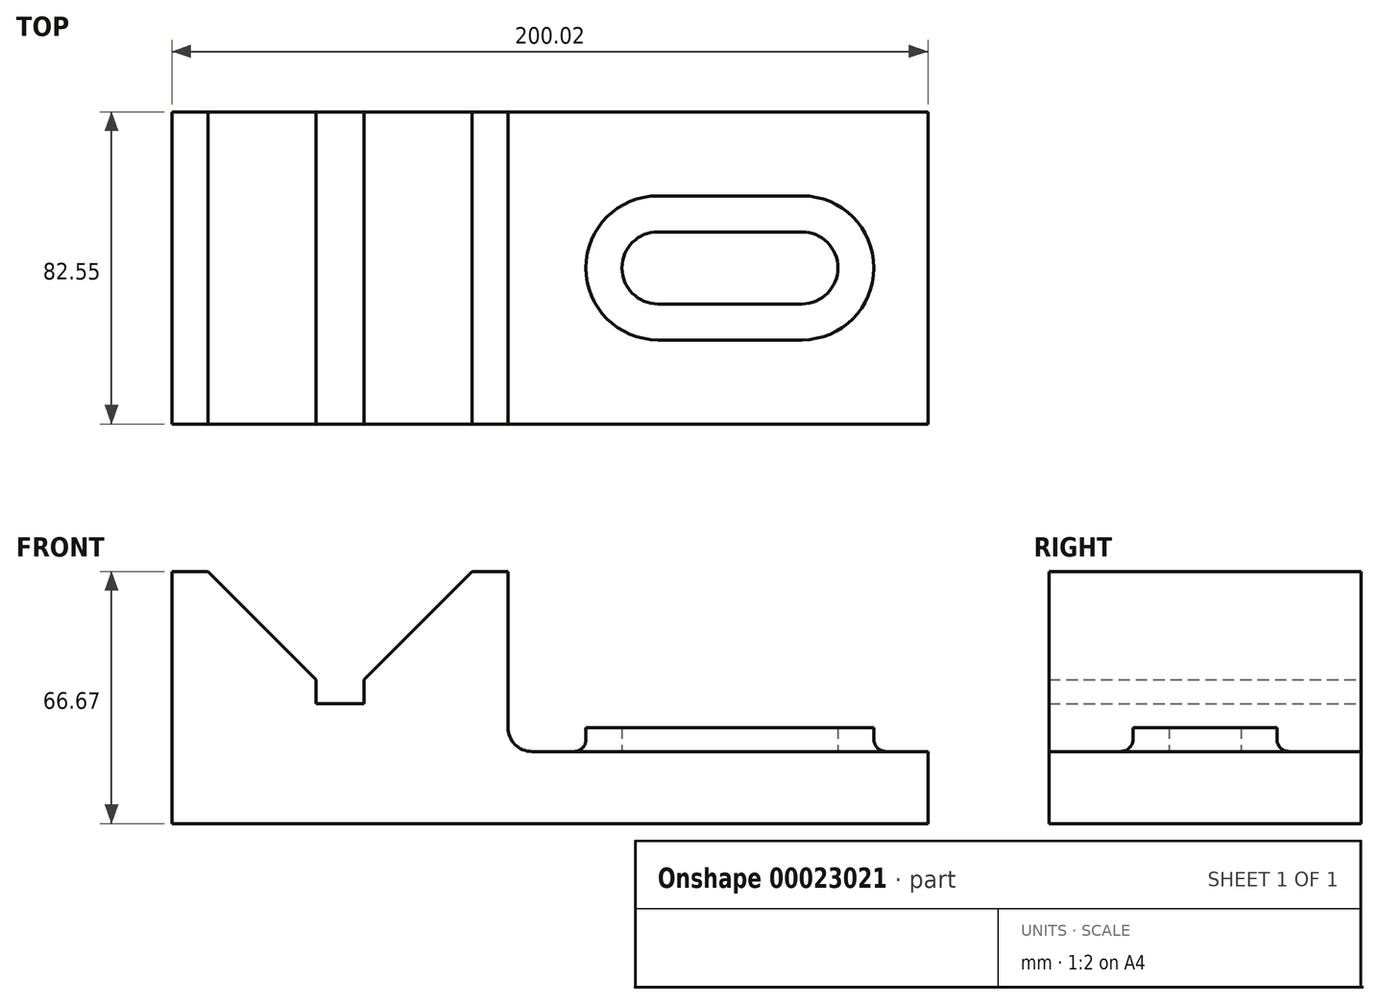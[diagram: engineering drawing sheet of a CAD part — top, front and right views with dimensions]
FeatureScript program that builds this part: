
annotation { "Feature Type Name" : "Feature", "Feature Type Description" : "" }
export const myFeature = defineFeature(function(context is Context, id is Id, definition is map)
    precondition{}
    {
        {
            var Q0;
            Q0=qCreatedBy(makeId("Front.planeOp"),FACE);
            var sketch = newSketch(context, id + "F0", { "sketchPlane" : qUnion([Q0])});
            skLineSegment(sketch, "E0", {"start": v(-103.64, -19.05) * mm, "end": v(96.38, -19.05) * mm});
            skLineSegment(sketch, "E1", {"start": v(-103.64, -19.05) * mm, "end": v(-103.64, 47.63) * mm});
            skLineSegment(sketch, "E2", {"start": v(-103.64, 47.63) * mm, "end": v(-94.12, 47.63) * mm});
            skLineSegment(sketch, "E3", {"start": v(-94.12, 47.63) * mm, "end": v(-24.27, 47.63) * mm});
            skLineSegment(sketch, "E4", {"start": v(-24.27, 47.63) * mm, "end": v(-14.74, 47.63) * mm});
            skLineSegment(sketch, "E5.bottom", {"start": v(-94.12, 47.63) * mm, "end": v(-65.54, 47.63) * mm});
            skLineSegment(sketch, "E5.top", {"start": v(-94.12, 19.05) * mm, "end": v(-65.54, 19.05) * mm});
            skLineSegment(sketch, "E5.left", {"start": v(-94.12, 47.63) * mm, "end": v(-94.12, 19.05) * mm});
            skLineSegment(sketch, "E6", {"start": v(-94.12, 47.63) * mm, "end": v(-65.54, 19.05) * mm});
            skLineSegment(sketch, "E7", {"start": v(-65.54, 19.05) * mm, "end": v(-65.54, 12.7) * mm});
            skLineSegment(sketch, "E8", {"start": v(-65.54, 12.7) * mm, "end": v(-52.84, 12.7) * mm});
            skLineSegment(sketch, "E9", {"start": v(-52.84, 12.7) * mm, "end": v(-52.84, 19.05) * mm});
            skLineSegment(sketch, "E10.bottom", {"start": v(-52.84, 19.05) * mm, "end": v(-24.27, 19.05) * mm});
            skLineSegment(sketch, "E10.top", {"start": v(-52.84, 47.63) * mm, "end": v(-24.27, 47.63) * mm});
            skLineSegment(sketch, "E10.right", {"start": v(-24.27, 19.05) * mm, "end": v(-24.27, 47.63) * mm});
            skLineSegment(sketch, "E11", {"start": v(-52.84, 19.05) * mm, "end": v(-24.27, 47.63) * mm});
            skLineSegment(sketch, "E12", {"start": v(96.38, -19.05) * mm, "end": v(96.38, 0) * mm});
            skLineSegment(sketch, "E13", {"start": v(-14.74, 47.63) * mm, "end": v(-14.74, 0) * mm});
            skLineSegment(sketch, "E14", {"start": v(-14.74, 0) * mm, "end": v(96.38, 0) * mm});
            skSolve(sketch);
        }
        {
            var Q0;
            Q0=makeQuery(id+"F0.imprint","IMPRINT",FACE,{"disambiguationData":[TD([[makeQuery(id+"F0.imprint","IMPRINT",EDGE,{"derivedFrom":sQuery(id+"F0.wireOp",EDGE,"E0")}),1.0]])]});
            var Q1;
            Q1=makeQuery(id+"F0.imprint","IMPRINT",FACE,{"disambiguationData":[TD([[makeQuery(id+"F0.imprint","IMPRINT",EDGE,{"derivedFrom":sQuery(id+"F0.wireOp",EDGE,"E5.top")}),1.0]])]});
            var Q2;
            Q2=makeQuery(id+"F0.imprint","IMPRINT",FACE,{"disambiguationData":[TD([[makeQuery(id+"F0.imprint","IMPRINT",EDGE,{"derivedFrom":sQuery(id+"F0.wireOp",EDGE,"E10.bottom")}),1.0]])]});
            extrude(context, id + "F1", {"entities" : qUnion([Q0, Q1, Q2]), "depth" : 82.55 * mm});
        }
        {
            var Q0;
            Q0=makeQuery(id+"F1.opExtrude","SWEPT_EDGE",EDGE,{"disambiguationData":[OSD([sQuery(id+"F0.wireOp",EDGE,"E13"),sQuery(id+"F0.wireOp",EDGE,"E14")])]});
            fillet(context, id + "F2", {"entities" : qUnion([Q0]), "radius" : 6.35 * mm, "tangentPropagation" : true, "allowEdgeOverflow" : false});
        }
        {
            var Q0;
            Q0=makeQuery(id+"F1.opExtrude","SWEPT_FACE",FACE,{"disambiguationData":[OSD([sQuery(id+"F0.wireOp",EDGE,"E14")])]});
            var sketch = newSketch(context, id + "F3", { "sketchPlane" : qUnion([Q0])});
            skLineSegment(sketch, "E15", {"start": v(96.38, -82.55) * mm, "end": v(96.38, 0) * mm});
            skPoint(sketch, "E16", {"position": v(96.38, -41.28) * mm});
            skArc(sketch, "E17", {"start": v(24.94, -31.75) * mm, "mid": v(15.42, -41.28) * mm, "end": v(24.94, -50.8) * mm});
            skArc(sketch, "E18", {"start": v(63.04, -50.8) * mm, "mid": v(72.57, -41.28) * mm, "end": v(63.04, -31.75) * mm});
            skArc(sketch, "E19", {"start": v(24.94, -22.23) * mm, "mid": v(5.9, -41.28) * mm, "end": v(24.94, -60.33) * mm});
            skArc(sketch, "E20", {"start": v(63.04, -60.33) * mm, "mid": v(82.1, -41.28) * mm, "end": v(63.04, -22.23) * mm});
            skLineSegment(sketch, "E21", {"start": v(24.94, -60.33) * mm, "end": v(63.04, -60.33) * mm});
            skLineSegment(sketch, "E22", {"start": v(63.04, -22.23) * mm, "end": v(24.94, -22.23) * mm});
            skLineSegment(sketch, "E23", {"start": v(24.94, -50.8) * mm, "end": v(63.04, -50.8) * mm});
            skLineSegment(sketch, "E24", {"start": v(24.94, -31.75) * mm, "end": v(63.04, -31.75) * mm});
            skPoint(sketch, "E25.start.orphan", {"position": v(-8.4, -41.28) * mm});
            skSolve(sketch);
        }
        {
            var Q0;
            Q0=makeQuery(id+"F3.imprint","IMPRINT",FACE,{"disambiguationData":[TD([[makeQuery(id+"F3.imprint","IMPRINT",EDGE,{"derivedFrom":sQuery(id+"F3.wireOp",EDGE,"E17")}),-1.0]])]});
            extrude(context, id + "F4", {"entities" : qUnion([Q0]), "operationType" : NewBodyOperationType.ADD, "depth" : 6.35 * mm});
        }
        {
            var Q0;
            Q0=makeQuery(id+"F4.opExtrude","CAP_EDGE",EDGE,{"disambiguationData":[OSD([sQuery(id+"F3.wireOp",EDGE,"E22")])],"isStart":true});
            fillet(context, id + "F5", {"entities" : qUnion([Q0]), "radius" : 3.17 * mm, "tangentPropagation" : true, "allowEdgeOverflow" : false});
        }
    });
